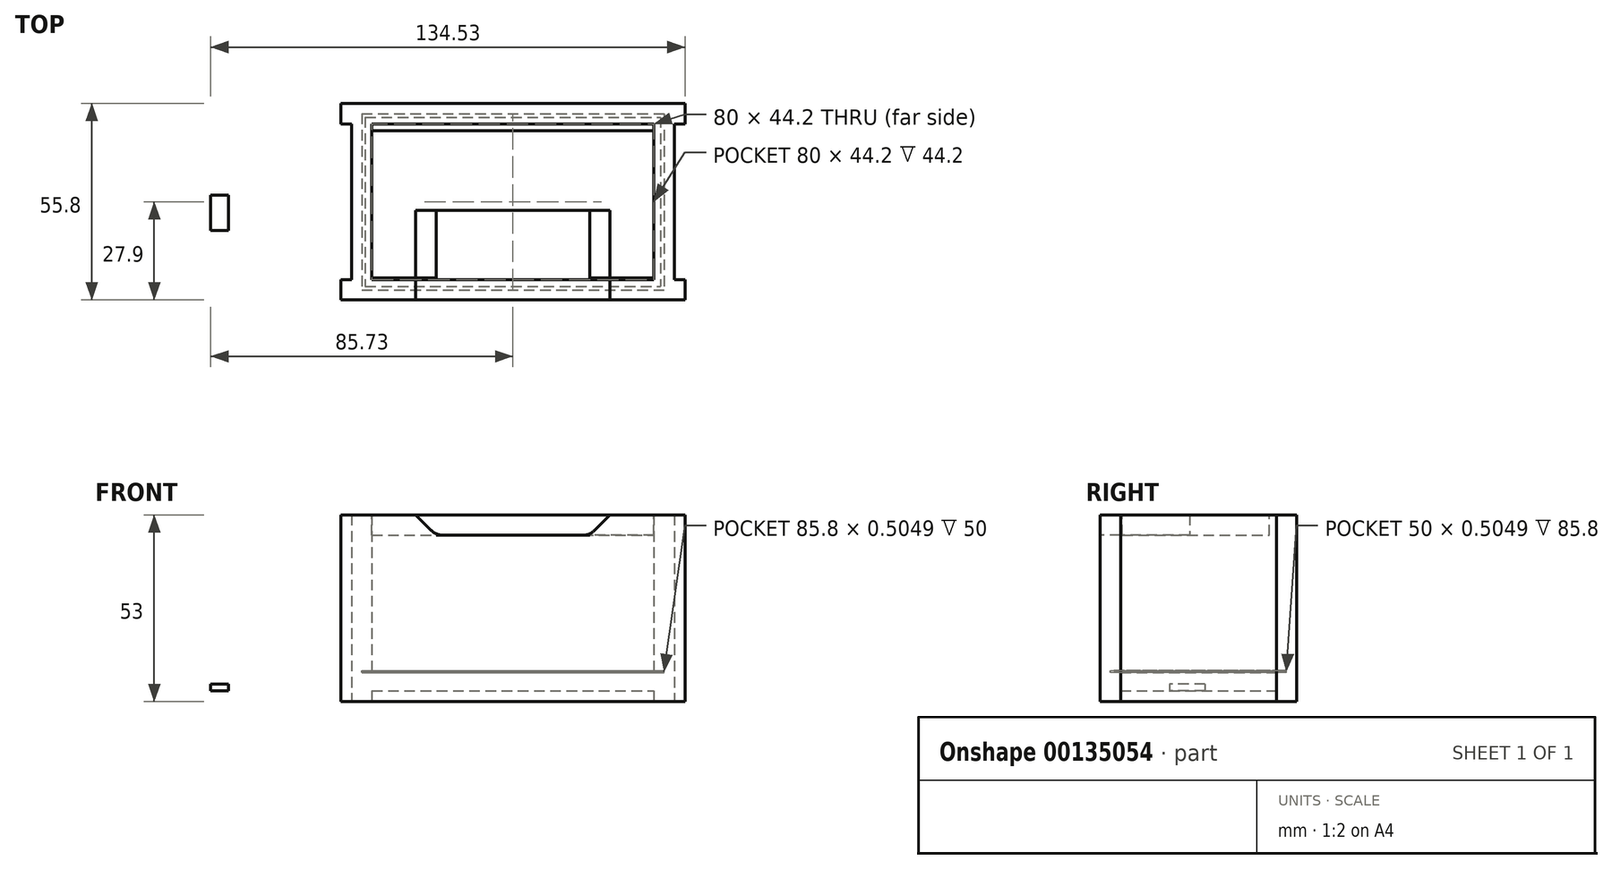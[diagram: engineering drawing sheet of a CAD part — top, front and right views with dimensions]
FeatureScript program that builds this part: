
annotation { "Feature Type Name" : "Feature", "Feature Type Description" : "" }
export const myFeature = defineFeature(function(context is Context, id is Id, definition is map)
    precondition{}
    {
        {
            assignVariable(context, id + "F0", {"name" : "wallThick", "anyValue" : 5.8 * mm});
        }
        {
            assignVariable(context, id + "F1", {"name" : "boxHeight", "anyValue" : 50 * mm});
        }
        {
            assignVariable(context, id + "F2", {"name" : "tol", "anyValue" : 3 * mm});
        }
        {
            assignVariable(context, id + "F3", {"name" : "bottomSlotThick", "anyValue" : 1 / 203.2 * mm + .5 * mm});
        }
        {
            assignVariable(context, id + "F4", {"name" : "bottomTabThick", "anyValue" : 1 / 203.2 * mm + .2 * mm});
        }
        {
            var Q0;
            Q0=qCreatedBy(makeId("Top.planeOp"),FACE);
            var sketch = newSketch(context, id + "F5", { "sketchPlane" : qUnion([Q0])});
            skLineSegment(sketch, "E0", {"start": v(-25.02, 0) * mm, "end": v(25.86, 0) * mm, "construction": true});
            skLineSegment(sketch, "E1", {"start": v(0, -15.52) * mm, "end": v(0, 21.88) * mm, "construction": true});
            skLineSegment(sketch, "E2.bottom", {"start": v(-45.8, -22.1) * mm, "end": v(-40, -22.1) * mm});
            skLineSegment(sketch, "E2.top", {"start": v(-45.8, 22.1) * mm, "end": v(-40, 22.1) * mm});
            skLineSegment(sketch, "E2.left", {"start": v(-45.8, -22.1) * mm, "end": v(-45.8, 22.1) * mm});
            skLineSegment(sketch, "E2.right", {"start": v(-40, -22.1) * mm, "end": v(-40, 22.1) * mm});
            skLineSegment(sketch, "E3.bottom", {"start": v(-48.8, -27.9) * mm, "end": v(48.8, -27.9) * mm});
            skLineSegment(sketch, "E3.top", {"start": v(-48.8, -22.1) * mm, "end": v(48.8, -22.1) * mm});
            skLineSegment(sketch, "E3.left", {"start": v(-48.8, -27.9) * mm, "end": v(-48.8, -22.1) * mm});
            skLineSegment(sketch, "E3.right", {"start": v(48.8, -27.9) * mm, "end": v(48.8, -22.1) * mm});
            skLineSegment(sketch, "E4.MirrorCS", {"start": v(-48.8, 27.9) * mm, "end": v(48.8, 27.9) * mm});
            skLineSegment(sketch, "E5.MirrorCS", {"start": v(-48.8, 27.9) * mm, "end": v(-48.8, 22.1) * mm});
            skLineSegment(sketch, "E6.MirrorCS", {"start": v(-48.8, 22.1) * mm, "end": v(48.8, 22.1) * mm});
            skLineSegment(sketch, "E7.MirrorCS", {"start": v(48.8, 27.9) * mm, "end": v(48.8, 22.1) * mm});
            skLineSegment(sketch, "E8.MirrorCS", {"start": v(45.8, -22.1) * mm, "end": v(45.8, 22.1) * mm});
            skLineSegment(sketch, "E9.MirrorCS", {"start": v(40, -22.1) * mm, "end": v(40, 22.1) * mm});
            skLineSegment(sketch, "E10.top", {"start": v(-45.8, 25) * mm, "end": v(-40, 25) * mm});
            skLineSegment(sketch, "E10.left", {"start": v(-45.8, 22.1) * mm, "end": v(-45.8, 25) * mm});
            skLineSegment(sketch, "E10.right", {"start": v(-40, 22.1) * mm, "end": v(-40, 25) * mm});
            skLineSegment(sketch, "E11.MirrorCS", {"start": v(45.8, 25) * mm, "end": v(40, 25) * mm});
            skLineSegment(sketch, "E12.MirrorCS", {"start": v(40, 22.1) * mm, "end": v(40, 25) * mm});
            skLineSegment(sketch, "E13.MirrorCS", {"start": v(45.8, 22.1) * mm, "end": v(45.8, 25) * mm});
            skLineSegment(sketch, "E14.MirrorCS", {"start": v(40, -22.1) * mm, "end": v(40, -25) * mm});
            skLineSegment(sketch, "E15.MirrorCS", {"start": v(45.8, -22.1) * mm, "end": v(45.8, -25) * mm});
            skLineSegment(sketch, "E16.MirrorCS", {"start": v(45.8, -25) * mm, "end": v(40, -25) * mm});
            skLineSegment(sketch, "E17.MirrorCS", {"start": v(-45.8, -22.1) * mm, "end": v(-45.8, -25) * mm});
            skLineSegment(sketch, "E18.MirrorCS", {"start": v(-45.8, -25) * mm, "end": v(-40, -25) * mm});
            skLineSegment(sketch, "E19.MirrorCS", {"start": v(-40, -22.1) * mm, "end": v(-40, -25) * mm});
            skSolve(sketch);
        }
        {
            var Q0;
            Q0=makeQuery(id+"F5.imprint","IMPRINT",FACE,{"disambiguationData":[TD([[makeQuery(id+"F5.imprint","IMPRINT",EDGE,{"derivedFrom":sQuery(id+"F5.wireOp",EDGE,"E4.MirrorCS")}),-1.0]])]});
            var Q1;
            Q1=makeQuery(id+"F5.imprint","IMPRINT",FACE,{"disambiguationData":[TD([[makeQuery(id+"F5.imprint","IMPRINT",EDGE,{"derivedFrom":sQuery(id+"F5.wireOp",EDGE,"E3.bottom")}),1.0]])]});
            extrude(context, id + "F6", {"entities" : qUnion([Q0, Q1]), "depth" : getVariable(context, 'boxHeight'), "hasSecondDirection" : true, "secondDirectionOppositeDirection" : true, "secondDirectionDepth" : getVariable(context, 'tol')});
        }
        {
            var Q0;
            Q0=makeQuery(id+"F5.imprint","IMPRINT",FACE,{"disambiguationData":[TD([[makeQuery(id+"F5.imprint","IMPRINT",EDGE,{"derivedFrom":sQuery(id+"F5.wireOp",EDGE,"E2.top")}),1.0]])]});
            var Q1;
            {var subQ0=sQuery(id+"F5.wireOp",EDGE,"E2.left");Q1=makeQuery(id+"F5.imprint","IMPRINT",FACE,{"disambiguationData":[TD([[makeQuery(id+"F5.imprint","IMPRINT",EDGE,{"derivedFrom":subQ0}),-1.0]])]});}
            var Q2;
            {var subQ0=sQuery(id+"F5.wireOp",EDGE,"E17.MirrorCS");Q2=makeQuery(id+"F5.imprint","IMPRINT",FACE,{"disambiguationData":[TD([[makeQuery(id+"F5.imprint","IMPRINT",EDGE,{"derivedFrom":subQ0}),1.0]])]});}
            var Q3;
            Q3=makeQuery(id+"F5.imprint","IMPRINT",FACE,{"disambiguationData":[TD([[makeQuery(id+"F5.imprint","IMPRINT",EDGE,{"derivedFrom":sQuery(id+"F5.wireOp",EDGE,"E11.MirrorCS")}),1.0]])]});
            var Q4;
            {var subQ0=sQuery(id+"F5.wireOp",EDGE,"E8.MirrorCS");Q4=makeQuery(id+"F5.imprint","IMPRINT",FACE,{"disambiguationData":[TD([[makeQuery(id+"F5.imprint","IMPRINT",EDGE,{"derivedFrom":subQ0}),1.0]])]});}
            var Q5;
            {var subQ2=sQuery(id+"F5.wireOp",EDGE,"E14.MirrorCS");Q5=makeQuery(id+"F5.imprint","IMPRINT",FACE,{"disambiguationData":[TD([[makeQuery(id+"F5.imprint","IMPRINT",EDGE,{"derivedFrom":subQ2}),1.0]])]});}
            extrude(context, id + "F7", {"entities" : qUnion([Q0, Q1, Q2, Q3, Q4, Q5]), "depth" : getVariable(context, 'boxHeight'), "hasSecondDirection" : true, "secondDirectionOppositeDirection" : true, "secondDirectionDepth" : getVariable(context, 'tol')});
        }
        {
            var Q0;
            {var subQ0=sQuery(id+"F5.wireOp",EDGE,"E2.right");Q0=makeQuery(id+"F5.imprint","IMPRINT",FACE,{"disambiguationData":[TD([[makeQuery(id+"F5.imprint","IMPRINT",EDGE,{"derivedFrom":subQ0}),-1.0]])]});}
            extrude(context, id + "F8", {"entities" : qUnion([Q0]), "depth" : getVariable(context, 'wallThick')});
        }
        {
            var Q0;
            Q0=makeQuery(id+"F8.opExtrude","CAP_FACE",FACE,{"disambiguationData":[OSD([sQuery(id+"F5.wireOp",EDGE,"E2.right"),sQuery(id+"F5.wireOp",EDGE,"E3.top"),sQuery(id+"F5.wireOp",EDGE,"E6.MirrorCS"),sQuery(id+"F5.wireOp",EDGE,"E9.MirrorCS")])],"isStart":false});
            var sketch = newSketch(context, id + "F9", { "sketchPlane" : qUnion([Q0])});
            skLineSegment(sketch, "E20.bottom", {"start": v(-42.9, 25) * mm, "end": v(42.9, 25) * mm});
            skLineSegment(sketch, "E20.top", {"start": v(-42.9, -25) * mm, "end": v(42.9, -25) * mm});
            skLineSegment(sketch, "E20.left", {"start": v(-42.9, 25) * mm, "end": v(-42.9, -25) * mm});
            skLineSegment(sketch, "E20.right", {"start": v(42.9, 25) * mm, "end": v(42.9, -25) * mm});
            skLineSegment(sketch, "E21.bottom", {"start": v(-41.9, 24) * mm, "end": v(41.9, 24) * mm});
            skLineSegment(sketch, "E21.top", {"start": v(-41.9, -24) * mm, "end": v(41.9, -24) * mm});
            skLineSegment(sketch, "E21.left", {"start": v(-41.9, 24) * mm, "end": v(-41.9, -24) * mm});
            skLineSegment(sketch, "E21.right", {"start": v(41.9, 24) * mm, "end": v(41.9, -24) * mm});
            skSolve(sketch);
        }
        {
            var Q0;
            Q0=makeQuery(id+"F9.imprint","IMPRINT",FACE,{"disambiguationData":[TD([[makeQuery(id+"F9.imprint","IMPRINT",EDGE,{"derivedFrom":sQuery(id+"F9.wireOp",EDGE,"E20.bottom")}),-1.0]])]});
            var Q1;
            Q1=makeQuery(id+"F9.imprint","IMPRINT",FACE,{"disambiguationData":[TD([[makeQuery(id+"F9.imprint","IMPRINT",EDGE,{"derivedFrom":sQuery(id+"F9.wireOp",EDGE,"E21.bottom")}),-1.0]])]});
            extrude(context, id + "F10", {"entities" : qUnion([Q0, Q1]), "operationType" : NewBodyOperationType.REMOVE, "oppositeDirection" : true, "depth" : getVariable(context, 'bottomSlotThick')});
        }
        {
            var Q0;
            Q0=makeQuery(id+"F9.imprint","IMPRINT",FACE,{"disambiguationData":[TD([[makeQuery(id+"F9.imprint","IMPRINT",EDGE,{"derivedFrom":sQuery(id+"F9.wireOp",EDGE,"E21.bottom")}),-1.0]])]});
            extrude(context, id + "F11", {"entities" : qUnion([Q0]), "operationType" : NewBodyOperationType.ADD, "oppositeDirection" : true, "depth" : getVariable(context, 'bottomTabThick')});
        }
        {
            var Q0;
            Q0=makeQuery(id+"F7.opExtrude","CAP_FACE",FACE,{"disambiguationData":[OSD([sQuery(id+"F5.wireOp",EDGE,"E2.left"),sQuery(id+"F5.wireOp",EDGE,"E2.right"),sQuery(id+"F5.wireOp",EDGE,"E10.top"),sQuery(id+"F5.wireOp",EDGE,"E10.left"),sQuery(id+"F5.wireOp",EDGE,"E10.right"),sQuery(id+"F5.wireOp",EDGE,"E17.MirrorCS"),sQuery(id+"F5.wireOp",EDGE,"E18.MirrorCS"),sQuery(id+"F5.wireOp",EDGE,"E19.MirrorCS")])],"isStart":false});
            var sketch = newSketch(context, id + "F12", { "sketchPlane" : qUnion([Q0])});
            skLineSegment(sketch, "E22.bottom", {"start": v(-40, 20.1) * mm, "end": v(40, 20.1) * mm});
            skLineSegment(sketch, "E22.left", {"start": v(-40, 20.1) * mm, "end": v(-40, -21.6) * mm});
            skLineSegment(sketch, "E22.right", {"start": v(40, 20.1) * mm, "end": v(40, -22.1) * mm});
            skLineSegment(sketch, "E23", {"start": v(-40, -21.6) * mm, "end": v(-18.12, -21.6) * mm});
            skLineSegment(sketch, "E24", {"start": v(-18.12, -21.6) * mm, "end": v(-11.82, -27.9) * mm});
            skLineSegment(sketch, "E25", {"start": v(-11.82, -27.9) * mm, "end": v(0, -27.9) * mm});
            skLineSegment(sketch, "E26.MirrorCS", {"start": v(40, -21.6) * mm, "end": v(18.12, -21.6) * mm});
            skLineSegment(sketch, "E27.MirrorCS", {"start": v(18.12, -21.6) * mm, "end": v(11.82, -27.9) * mm});
            skLineSegment(sketch, "E28.MirrorCS", {"start": v(11.82, -27.9) * mm, "end": v(0, -27.9) * mm});
            skSolve(sketch);
        }
        {
            var Q0;
            {var subQ1=sQuery(id+"F12.wireOp",EDGE,"E22.bottom");Q0=makeQuery(id+"F12.imprint","IMPRINT",FACE,{"disambiguationData":[TD([[makeQuery(id+"F12.imprint","IMPRINT",EDGE,{"derivedFrom":subQ1}),-1.0]])]});}
            extrude(context, id + "F13", {"entities" : qUnion([Q0]), "oppositeDirection" : true, "depth" : getVariable(context, 'wallThick')});
        }
        {
            var Q0;
            Q0=makeQuery(id+"F6.opExtrude","SWEPT_FACE",FACE,{"disambiguationData":[OSD([sQuery(id+"F5.wireOp",EDGE,"E3.bottom")])]});
            var sketch = newSketch(context, id + "F14", { "sketchPlane" : qUnion([Q0])});
            skLineSegment(sketch, "E29", {"start": v(-27.55, 50) * mm, "end": v(-21.75, 44.2) * mm});
            skLineSegment(sketch, "E30", {"start": v(-21.75, 44.2) * mm, "end": v(0, 44.2) * mm});
            skLineSegment(sketch, "E31", {"start": v(-27.55, 50) * mm, "end": v(0, 50) * mm});
            skLineSegment(sketch, "E32.MirrorCS", {"start": v(21.75, 44.2) * mm, "end": v(0, 44.2) * mm});
            skLineSegment(sketch, "E33.MirrorCS", {"start": v(27.55, 50) * mm, "end": v(21.75, 44.2) * mm});
            skLineSegment(sketch, "E34.MirrorCS", {"start": v(27.55, 50) * mm, "end": v(0, 50) * mm});
            skSolve(sketch);
        }
        {
            var Q0;
            Q0 = qSketchRegion(id + "F14", true);
            extrude(context, id + "F15", {"entities" : qUnion([Q0]), "operationType" : NewBodyOperationType.REMOVE, "oppositeDirection" : true, "depth" : 25.4 * mm});
        }
        {
            var Q0;
            Q0=makeQuery(id+"F15.boolean.opBoolean","COPY",EDGE,{"derivedFrom":makeQuery(id+"F15.opExtrude","SWEPT_EDGE",EDGE,{"disambiguationData":[OSD([sQuery(id+"F5.wireOp",EDGE,"E3.bottom"),sQuery(id+"F14.wireOp",EDGE,"E29"),sQuery(id+"F14.wireOp",EDGE,"E31")])]})});
            var Q1;
            Q1=makeQuery(id+"F15.boolean.opBoolean","COPY",EDGE,{"derivedFrom":makeQuery(id+"F15.opExtrude","SWEPT_EDGE",EDGE,{"disambiguationData":[OSD([sQuery(id+"F14.wireOp",EDGE,"E29"),sQuery(id+"F14.wireOp",EDGE,"E30")])]})});
            var Q2;
            Q2=makeQuery(id+"F15.boolean.opBoolean","COPY",EDGE,{"derivedFrom":makeQuery(id+"F15.opExtrude","SWEPT_EDGE",EDGE,{"disambiguationData":[OSD([sQuery(id+"F14.wireOp",EDGE,"E32.MirrorCS"),sQuery(id+"F14.wireOp",EDGE,"E33.MirrorCS")])]})});
            var Q3;
            Q3=makeQuery(id+"F15.boolean.opBoolean","COPY",EDGE,{"derivedFrom":makeQuery(id+"F15.opExtrude","SWEPT_EDGE",EDGE,{"disambiguationData":[OSD([sQuery(id+"F5.wireOp",EDGE,"E3.bottom"),sQuery(id+"F14.wireOp",EDGE,"E33.MirrorCS"),sQuery(id+"F14.wireOp",EDGE,"E34.MirrorCS")])]})});
            var Q4;
            Q4=makeQuery(id+"F13.opExtrude","SWEPT_EDGE",EDGE,{"disambiguationData":[OSD([sQuery(id+"F12.wireOp",EDGE,"E26.MirrorCS"),sQuery(id+"F12.wireOp",EDGE,"E27.MirrorCS")])]});
            var Q5;
            Q5=makeQuery(id+"F13.opExtrude","SWEPT_EDGE",EDGE,{"disambiguationData":[OSD([sQuery(id+"F12.wireOp",EDGE,"E27.MirrorCS"),sQuery(id+"F12.wireOp",EDGE,"E28.MirrorCS")])]});
            var Q6;
            Q6=makeQuery(id+"F13.opExtrude","SWEPT_EDGE",EDGE,{"disambiguationData":[OSD([sQuery(id+"F12.wireOp",EDGE,"E24"),sQuery(id+"F12.wireOp",EDGE,"E25")])]});
            var Q7;
            Q7=makeQuery(id+"F13.opExtrude","SWEPT_EDGE",EDGE,{"disambiguationData":[OSD([sQuery(id+"F12.wireOp",EDGE,"E23"),sQuery(id+"F12.wireOp",EDGE,"E24")])]});
            fillet(context, id + "F16", {"entities" : qUnion([Q0, Q1, Q2, Q3, Q4, Q5, Q6, Q7]), "radius" : 5.08 * mm, "tangentPropagation" : true, "allowEdgeOverflow" : false});
        }
        {
            var Q0;
            Q0=qCreatedBy(makeId("Top.planeOp"),FACE);
            var sketch = newSketch(context, id + "F17", { "sketchPlane" : qUnion([Q0])});
            skLineSegment(sketch, "E35.bottom", {"start": v(-80.73, 1.86) * mm, "end": v(-85.73, 1.86) * mm});
            skLineSegment(sketch, "E35.top", {"start": v(-80.73, -8.14) * mm, "end": v(-85.73, -8.14) * mm});
            skLineSegment(sketch, "E35.left", {"start": v(-80.73, 1.86) * mm, "end": v(-80.73, -8.14) * mm});
            skLineSegment(sketch, "E35.right", {"start": v(-85.73, 1.86) * mm, "end": v(-85.73, -8.14) * mm});
            skPoint(sketch, "E35.middle", {"position": v(-83.23, -3.14) * mm});
            skSolve(sketch);
        }
        {
            var Q0;
            Q0=makeQuery(id+"F17.imprint","IMPRINT",FACE,{"disambiguationData":[TD([[makeQuery(id+"F17.imprint","IMPRINT",EDGE,{"derivedFrom":sQuery(id+"F17.wireOp",EDGE,"E35.bottom")}),1.0]])]});
            extrude(context, id + "F18", {"entities" : qUnion([Q0]), "depth" : 2 * mm});
        }
    });
